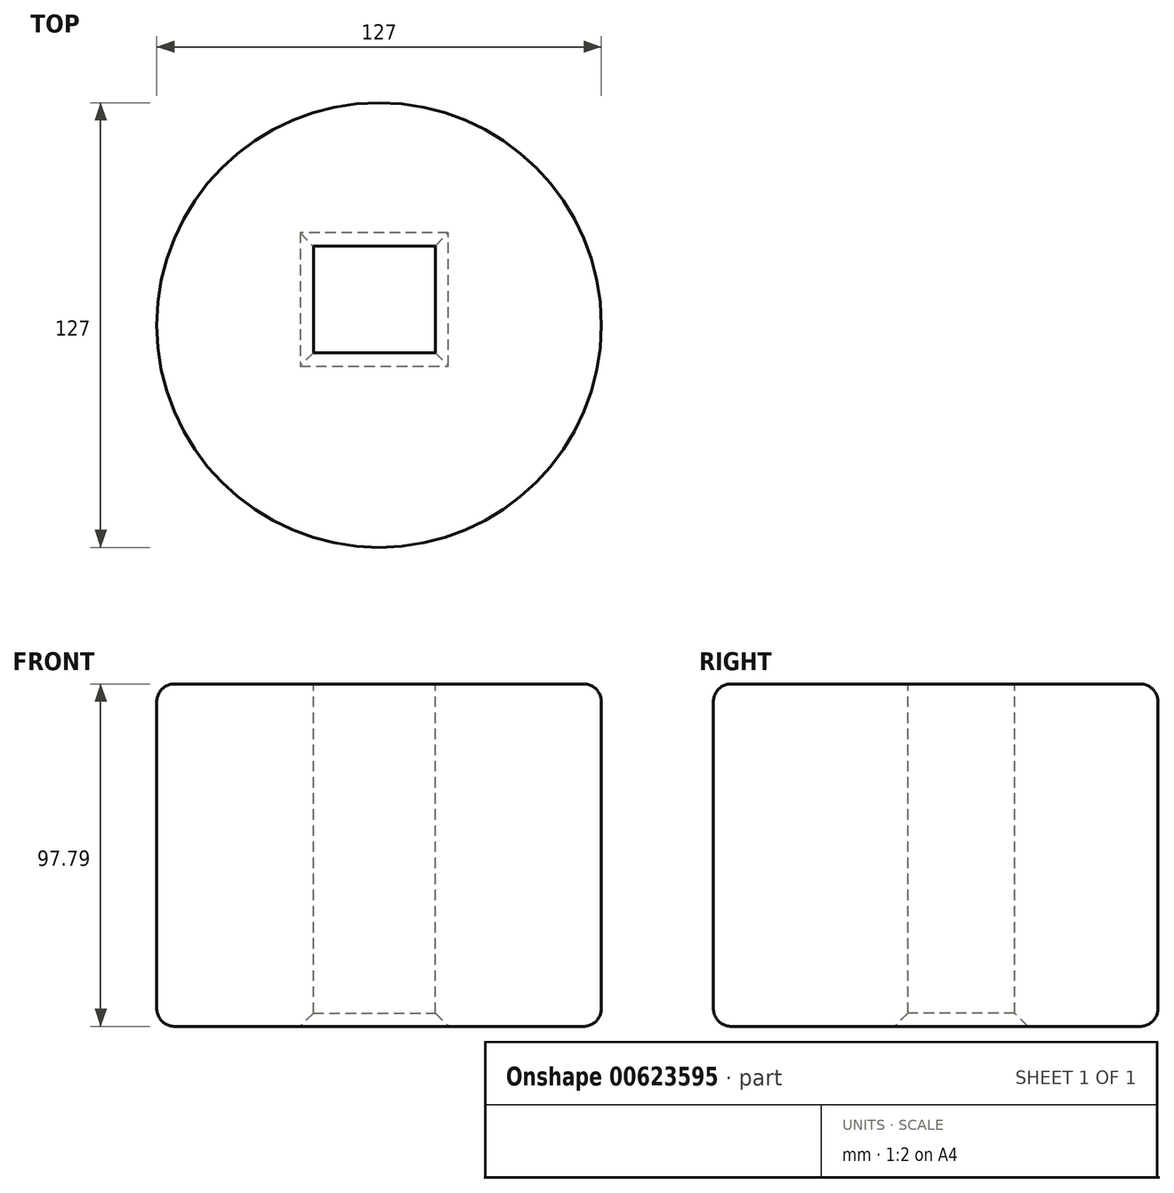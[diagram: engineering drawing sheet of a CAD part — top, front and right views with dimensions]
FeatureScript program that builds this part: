
annotation { "Feature Type Name" : "Feature", "Feature Type Description" : "" }
export const myFeature = defineFeature(function(context is Context, id is Id, definition is map)
    precondition{}
    {
        {
            var Q0;
            Q0=qCreatedBy(makeId("Top.planeOp"),FACE);
            var sketch = newSketch(context, id + "F0", { "sketchPlane" : qUnion([Q0])});
            skCircle(sketch, "E0", {"center": v(0, 0) * mm, "radius": 63.5 * mm});
            skSolve(sketch);
        }
        {
            var Q0;
            Q0 = qSketchRegion(id + "F0", true);
            extrude(context, id + "F1", {"entities" : qUnion([Q0]), "depth" : 97.8 * mm, "offsetDistance" : 25.4 * mm});
        }
        {
            var Q0;
            Q0=makeQuery(id+"F1.opExtrude","CAP_FACE",FACE,{"disambiguationData":[OSD([sQuery(id+"F0.wireOp",EDGE,"E0")])],"isStart":false});
            var sketch = newSketch(context, id + "F2", { "sketchPlane" : qUnion([Q0])});
            skLineSegment(sketch, "E1.bottom", {"start": v(16.04, 22.56) * mm, "end": v(-18.75, 22.56) * mm});
            skLineSegment(sketch, "E1.top", {"start": v(16.04, -7.88) * mm, "end": v(-18.75, -7.88) * mm});
            skLineSegment(sketch, "E1.left", {"start": v(16.04, 22.56) * mm, "end": v(16.04, -7.88) * mm});
            skLineSegment(sketch, "E1.right", {"start": v(-18.75, 22.56) * mm, "end": v(-18.75, -7.88) * mm});
            skSolve(sketch);
        }
        {
            var Q0;
            Q0 = qSketchRegion(id + "F2", true);
            extrude(context, id + "F3", {"entities" : qUnion([Q0]), "operationType" : NewBodyOperationType.REMOVE, "endBound" : BoundingType.THROUGH_ALL, "oppositeDirection" : true, "depth" : 25.4 * mm, "offsetDistance" : 25.4 * mm});
        }
        {
            var Q0;
            Q0=makeQuery(id+"F1.opExtrude","CAP_EDGE",EDGE,{"disambiguationData":[OSD([sQuery(id+"F0.wireOp",EDGE,"E0")])],"isStart":false});
            var Q1;
            Q1=makeQuery(id+"F1.opExtrude","CAP_EDGE",EDGE,{"disambiguationData":[OSD([sQuery(id+"F0.wireOp",EDGE,"E0")])],"isStart":true});
            fillet(context, id + "F4", {"entities" : qUnion([Q0, Q1]), "radius" : 5.08 * mm, "tangentPropagation" : true, "allowEdgeOverflow" : false});
        }
        {
            var Q0;
            Q0=makeQuery(id+"F3.boolean.opBoolean","INTERSECT",EDGE,{"derivedFrom":[makeQuery(id+"F1.opExtrude","CAP_FACE",FACE,{"disambiguationData":[OSD([sQuery(id+"F0.wireOp",EDGE,"E0")])],"isStart":true}),makeQuery(id+"F3.opExtrude","SWEPT_FACE",FACE,{"disambiguationData":[OSD([sQuery(id+"F2.wireOp",EDGE,"E1.top")])]})]});
            var Q1;
            Q1=makeQuery(id+"F3.boolean.opBoolean","INTERSECT",EDGE,{"derivedFrom":[makeQuery(id+"F1.opExtrude","CAP_FACE",FACE,{"disambiguationData":[OSD([sQuery(id+"F0.wireOp",EDGE,"E0")])],"isStart":true}),makeQuery(id+"F3.opExtrude","SWEPT_FACE",FACE,{"disambiguationData":[OSD([sQuery(id+"F2.wireOp",EDGE,"E1.left")])]})]});
            var Q2;
            Q2=makeQuery(id+"F3.boolean.opBoolean","INTERSECT",EDGE,{"derivedFrom":[makeQuery(id+"F1.opExtrude","CAP_FACE",FACE,{"disambiguationData":[OSD([sQuery(id+"F0.wireOp",EDGE,"E0")])],"isStart":true}),makeQuery(id+"F3.opExtrude","SWEPT_FACE",FACE,{"disambiguationData":[OSD([sQuery(id+"F2.wireOp",EDGE,"E1.bottom")])]})]});
            var Q3;
            Q3=makeQuery(id+"F3.boolean.opBoolean","INTERSECT",EDGE,{"derivedFrom":[makeQuery(id+"F1.opExtrude","CAP_FACE",FACE,{"disambiguationData":[OSD([sQuery(id+"F0.wireOp",EDGE,"E0")])],"isStart":true}),makeQuery(id+"F3.opExtrude","SWEPT_FACE",FACE,{"disambiguationData":[OSD([sQuery(id+"F2.wireOp",EDGE,"E1.right")])]})]});
            var Q4;
            Q4=makeQuery(id+"F3.boolean.opBoolean","COPY",EDGE,{"derivedFrom":makeQuery(id+"F3.opExtrude","CAP_EDGE",EDGE,{"disambiguationData":[OSD([sQuery(id+"F2.wireOp",EDGE,"E1.left")])],"isStart":true})});
            var Q5;
            Q5=makeQuery(id+"F3.boolean.opBoolean","COPY",EDGE,{"derivedFrom":makeQuery(id+"F3.opExtrude","CAP_EDGE",EDGE,{"disambiguationData":[OSD([sQuery(id+"F2.wireOp",EDGE,"E1.bottom")])],"isStart":true})});
            var Q6;
            Q6=makeQuery(id+"F3.boolean.opBoolean","COPY",EDGE,{"derivedFrom":makeQuery(id+"F3.opExtrude","CAP_EDGE",EDGE,{"disambiguationData":[OSD([sQuery(id+"F2.wireOp",EDGE,"E1.right")])],"isStart":true})});
            var Q7;
            Q7=makeQuery(id+"F3.boolean.opBoolean","COPY",EDGE,{"derivedFrom":makeQuery(id+"F3.opExtrude","CAP_EDGE",EDGE,{"disambiguationData":[OSD([sQuery(id+"F2.wireOp",EDGE,"E1.top")])],"isStart":true})});
            chamfer(context, id + "F5", {"entities" : qUnion([Q0, Q1, Q2, Q3, Q4, Q5, Q6, Q7]), "width" : 3.8 * mm, "tangentPropagation" : true});
        }
    });
